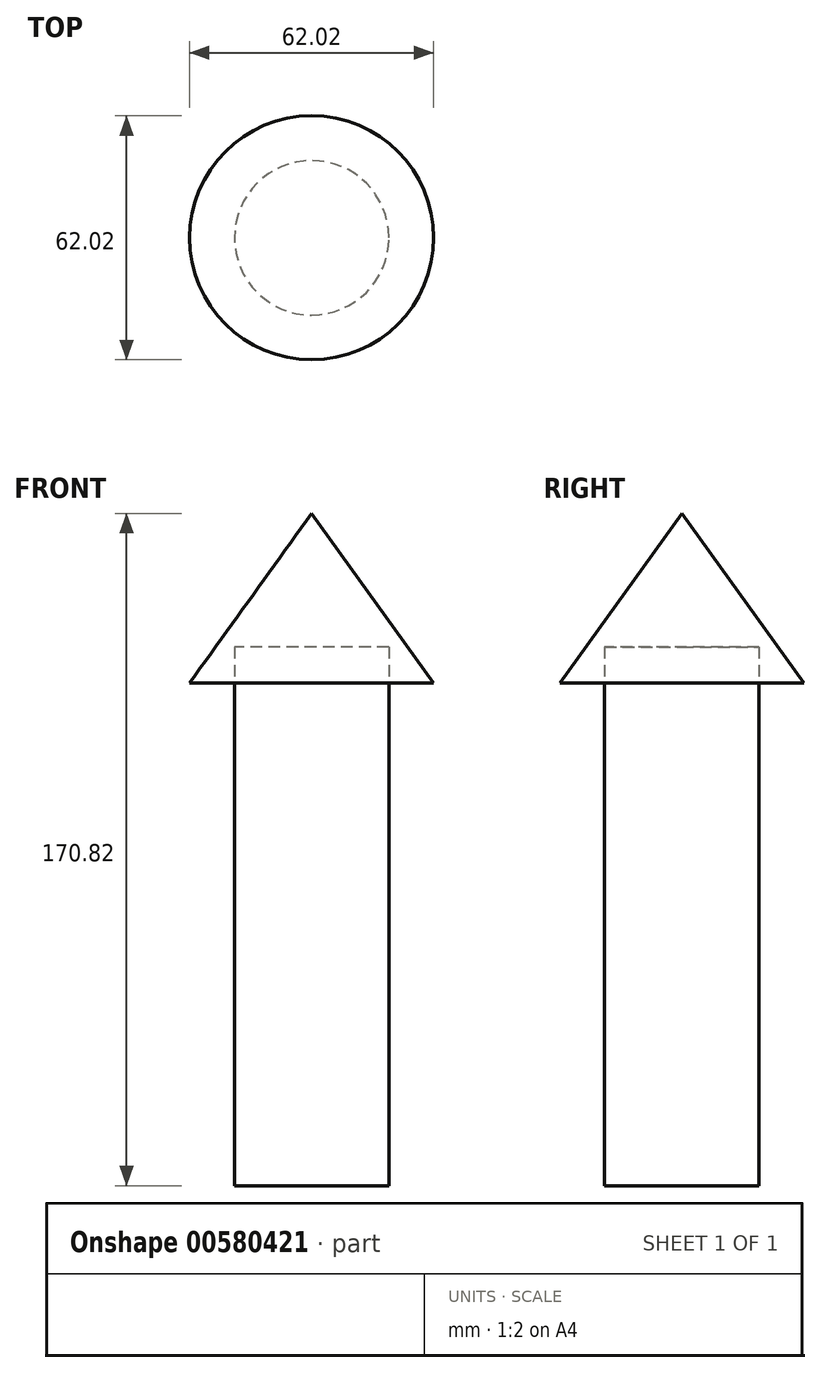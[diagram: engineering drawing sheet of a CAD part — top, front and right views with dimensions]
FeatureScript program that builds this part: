
annotation { "Feature Type Name" : "Feature", "Feature Type Description" : "" }
export const myFeature = defineFeature(function(context is Context, id is Id, definition is map)
    precondition{}
    {
        {
            var Q0;
            Q0=qCreatedBy(makeId("Top.planeOp"),FACE);
            var sketch = newSketch(context, id + "F0", { "sketchPlane" : qUnion([Q0])});
            skCircle(sketch, "E0", {"center": v(0, 0) * mm, "radius": 19.62 * mm});
            skSolve(sketch);
        }
        {
            var Q0;
            Q0 = qSketchRegion(id + "F0", true);
            extrude(context, id + "F1", {"entities" : qUnion([Q0]), "depth" : 111.5 * mm, "offsetDistance" : 25.4 * mm});
        }
        {
            var Q0;
            Q0=makeQuery(id+"F1.opExtrude","CAP_FACE",FACE,{"disambiguationData":[OSD([sQuery(id+"F0.wireOp",EDGE,"E0")])],"isStart":false});
            extrude(context, id + "F2", {"entities" : qUnion([Q0]), "operationType" : NewBodyOperationType.ADD, "depth" : 25.4 * mm, "offsetDistance" : 25.4 * mm});
        }
        {
            var Q0;
            Q0=qCreatedBy(makeId("Front.planeOp"),FACE);
            var sketch = newSketch(context, id + "F3", { "sketchPlane" : qUnion([Q0])});
            skLineSegment(sketch, "E1", {"start": v(0, 127.71) * mm, "end": v(19.44, 127.71) * mm});
            skLineSegment(sketch, "E2", {"start": v(0, 127.71) * mm, "end": v(0, 170.82) * mm});
            skLineSegment(sketch, "E3", {"start": v(19.44, 127.71) * mm, "end": v(31, 127.71) * mm});
            skLineSegment(sketch, "E4", {"start": v(31, 127.71) * mm, "end": v(0, 170.82) * mm});
            skSolve(sketch);
        }
        {
            var Q0;
            Q0=makeQuery(id+"F3.imprint","IMPRINT",FACE,{"disambiguationData":[TD([[makeQuery(id+"F3.imprint","IMPRINT",EDGE,{"derivedFrom":sQuery(id+"F3.wireOp",EDGE,"E1")}),1.0]])]});
            var Q1;
            Q1=sQuery(id+"F3.wireOp",EDGE,"E2");
            revolve(context, id + "F4", {"entities" : qUnion([Q0]), "axis" : qUnion([Q1]), "revolveType" : RevolveType.FULL});
        }
    });
